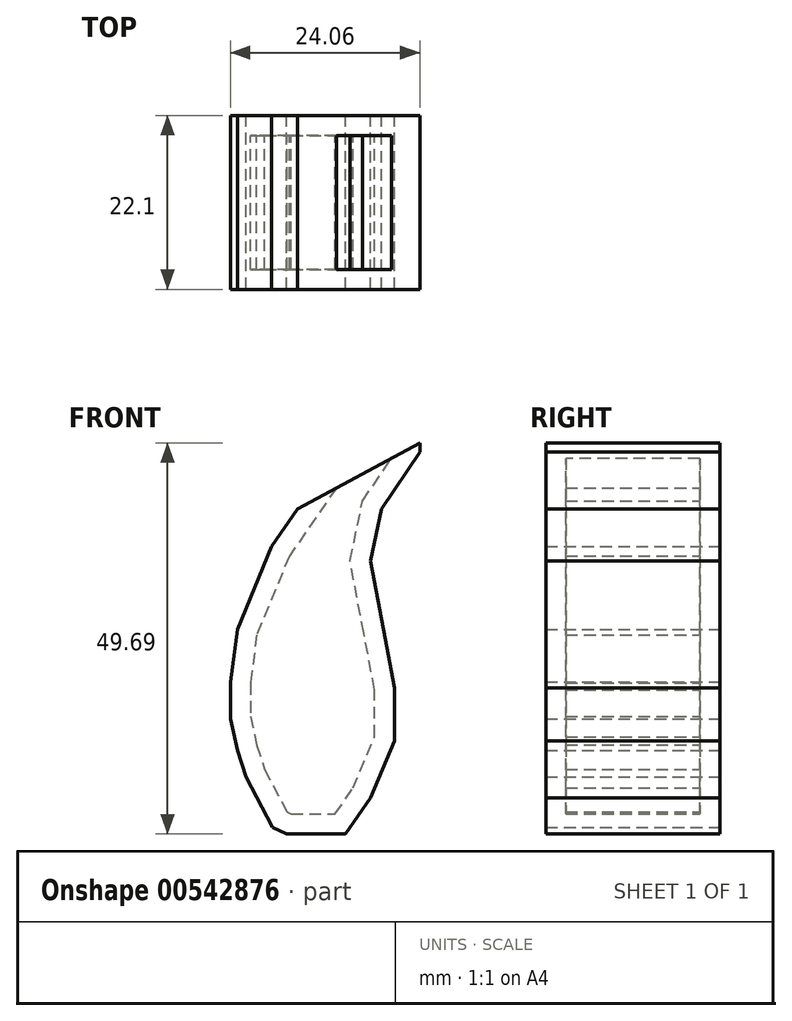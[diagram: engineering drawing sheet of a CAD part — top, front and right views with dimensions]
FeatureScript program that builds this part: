
annotation { "Feature Type Name" : "Feature", "Feature Type Description" : "" }
export const myFeature = defineFeature(function(context is Context, id is Id, definition is map)
    precondition{}
    {
        {
            var Q0;
            Q0=qCreatedBy(makeId("Front.planeOp"),FACE);
            var sketch = newSketch(context, id + "F0", { "sketchPlane" : qUnion([Q0])});
            skLineSegment(sketch, "E0", {"start": v(13.63, 25.9) * mm, "end": v(-1.88, 17.52) * mm});
            skLineSegment(sketch, "E1", {"start": v(-1.88, 17.52) * mm, "end": v(-5.2, 12.73) * mm});
            skLineSegment(sketch, "E2", {"start": v(-5.2, 12.73) * mm, "end": v(-9.56, 2.18) * mm});
            skLineSegment(sketch, "E3", {"start": v(-9.56, 2.18) * mm, "end": v(-10.43, -4.44) * mm});
            skLineSegment(sketch, "E4", {"start": v(-10.43, -4.44) * mm, "end": v(-10.43, -9.15) * mm});
            skLineSegment(sketch, "E5", {"start": v(-10.43, -9.15) * mm, "end": v(-9.56, -13.16) * mm});
            skLineSegment(sketch, "E6", {"start": v(-9.56, -13.16) * mm, "end": v(-8.42, -16.56) * mm});
            skLineSegment(sketch, "E7", {"start": v(-8.42, -16.56) * mm, "end": v(-5.11, -22.93) * mm});
            skLineSegment(sketch, "E8", {"start": v(-5.11, -22.93) * mm, "end": v(-3.28, -23.8) * mm});
            skLineSegment(sketch, "E9", {"start": v(-3.28, -23.8) * mm, "end": v(4.22, -23.8) * mm});
            skLineSegment(sketch, "E10", {"start": v(4.22, -23.8) * mm, "end": v(7.36, -19.18) * mm});
            skLineSegment(sketch, "E11", {"start": v(7.36, -19.18) * mm, "end": v(10.4, -11.94) * mm});
            skLineSegment(sketch, "E12", {"start": v(10.4, -11.94) * mm, "end": v(10.4, -9.85) * mm});
            skLineSegment(sketch, "E13", {"start": v(10.4, -9.85) * mm, "end": v(10.4, -5.23) * mm});
            skLineSegment(sketch, "E14", {"start": v(10.4, -5.23) * mm, "end": v(9.01, 2.18) * mm});
            skLineSegment(sketch, "E15", {"start": v(9.01, 2.18) * mm, "end": v(7.36, 10.9) * mm});
            skLineSegment(sketch, "E16", {"start": v(7.36, 10.9) * mm, "end": v(8.75, 17.52) * mm});
            skLineSegment(sketch, "E17", {"start": v(8.75, 17.52) * mm, "end": v(13.63, 24.76) * mm});
            skLineSegment(sketch, "E18", {"start": v(13.63, 24.76) * mm, "end": v(13.63, 25.9) * mm});
            skSolve(sketch);
        }
        {
            var Q0;
            Q0=makeQuery(id+"F0.imprint","IMPRINT",FACE,{"disambiguationData":[TD([[makeQuery(id+"F0.imprint","IMPRINT",EDGE,{"derivedFrom":sQuery(id+"F0.wireOp",EDGE,"E0")}),1.0]])]});
            extrude(context, id + "F1", {"entities" : qUnion([Q0]), "depth" : 22.1 * mm, "offsetDistance" : 25.4 * mm});
        }
        {
            var Q0;
            Q0=makeQuery(id+"F1.opExtrude","SWEPT_FACE",FACE,{"disambiguationData":[OSD([sQuery(id+"F0.wireOp",EDGE,"E0")])]});
            shell(context, id + "F2", {"entities" : qUnion([Q0]), "thickness" : 2.54 * mm});
        }
    });
